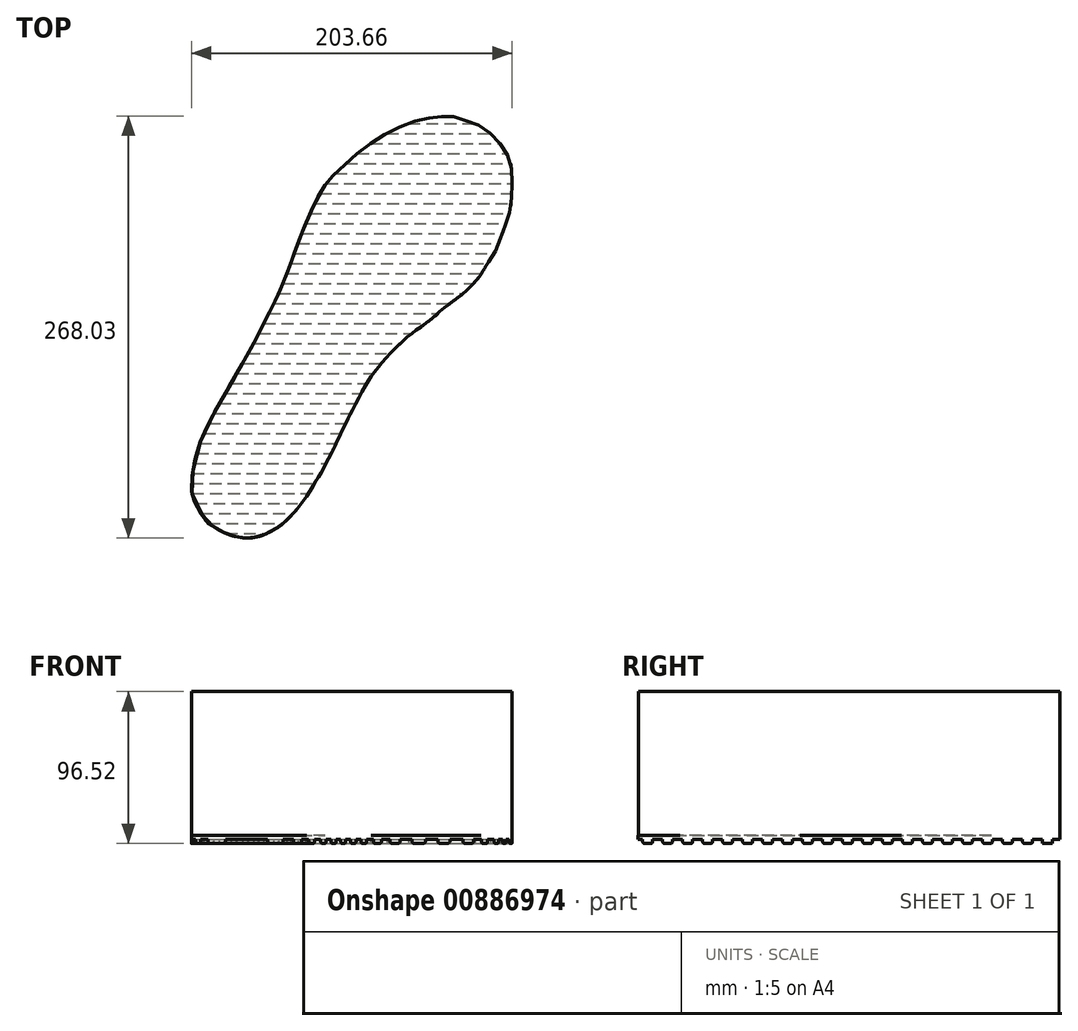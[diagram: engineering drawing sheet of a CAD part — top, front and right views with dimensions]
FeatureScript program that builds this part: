
annotation { "Feature Type Name" : "Feature", "Feature Type Description" : "" }
export const myFeature = defineFeature(function(context is Context, id is Id, definition is map)
    precondition{}
    {
        {
            var Q0;
            Q0=qCreatedBy(makeId("Top.planeOp"),FACE);
            var sketch = newSketch(context, id + "F0", { "sketchPlane" : qUnion([Q0])});
            skFitSpline(sketch, "E0", {"points": [v(-87.49, -126.78) * mm, v(-95.34, -113.93) * mm, v(-97.48, -103.22) * mm, v(-93.91, -82.03) * mm, v(-82.72, -56.56) * mm, v(-60.51, -17.71) * mm, v(-48.19, 6.35) * mm, v(-42.02, 18.83) * mm, v(-35.12, 35.9) * mm, v(-32.8, 42.2) * mm, v(-28.1, 54.9) * mm, v(-20.16, 73.8) * mm, v(-11.85, 88.53) * mm, v(-5.8, 94.95) * mm, v(5.91, 105.91) * mm, v(19.14, 115.74) * mm, v(32.74, 123.3) * mm, v(47.86, 128.96) * mm, v(57.68, 130.48) * mm, v(66.37, 131.23) * mm, v(75.06, 128.96) * mm, v(84.89, 125.56) * mm, v(94.34, 118.38) * mm, v(101.52, 109.7) * mm, v(105.67, 99.11) * mm, v(106.05, 86.64) * mm, v(105.3, 73.8) * mm, v(101.9, 61.7) * mm, v(97.74, 50.74) * mm, v(94.71, 43.94) * mm, v(89.8, 36.38) * mm, v(86.4, 30.71) * mm, v(78.68, 21.82) * mm, v(69.81, 14.52) * mm, v(62.51, 9.05) * mm, v(56.46, 3.57) * mm, v(49.99, -1.29) * mm, v(44.2, -5.6) * mm, v(38.26, -10.32) * mm, v(28.4, -19.8) * mm, v(23.09, -25.98) * mm, v(18.2, -32.02) * mm, v(14.32, -37.76) * mm, v(9.14, -47.04) * mm, v(4.13, -56.7) * mm, v(1.62, -61.71) * mm, v(-3.47, -72.08) * mm, v(-6.45, -78.5) * mm, v(-11.83, -88.97) * mm, v(-14.62, -94.55) * mm, v(-18.08, -99.93) * mm, v(-21.63, -106.17) * mm, v(-27.28, -114.4) * mm, v(-31.9, -120.26) * mm, v(-35.78, -124.24) * mm, v(-39.76, -127.85) * mm, v(-42.02, -129.57) * mm, v(-47.28, -132.82) * mm, v(-50.53, -134.39) * mm, v(-53.31, -135.42) * mm, v(-55.7, -135.96) * mm, v(-58.14, -136.5) * mm, v(-60.2, -136.64) * mm, v(-62.93, -136.75) * mm, v(-65.28, -136.57) * mm, v(-69, -135.92) * mm, v(-72.32, -135.07) * mm, v(-76.32, -133.55) * mm, v(-79.8, -131.88) * mm, v(-84.38, -128.96) * mm, v(-87.49, -126.78) * mm]});
            skSolve(sketch);
        }
        {
            var Q0;
            Q0=makeQuery(id+"F0.imprint","IMPRINT",FACE,{"disambiguationData":[TD([[makeQuery(id+"F0.imprint","IMPRINT",EDGE,{"derivedFrom":sQuery(id+"F0.wireOp",EDGE,"E0")}),-1.0]])]});
            extrude(context, id + "F1", {"entities" : qUnion([Q0]), "depth" : 91.44 * mm, "offsetDistance" : 25.4 * mm});
        }
        {
            var Q0;
            Q0=makeQuery(id+"F1.opExtrude","CAP_FACE",FACE,{"disambiguationData":[OSD([sQuery(id+"F0.wireOp",EDGE,"E0")])],"isStart":true});
            var sketch = newSketch(context, id + "F2", { "sketchPlane" : qUnion([Q0])});
            skLineSegment(sketch, "E1.bottom", {"start": v(-129.53, 140.32) * mm, "end": v(138.04, 140.32) * mm});
            skLineSegment(sketch, "E1.top", {"start": v(-129.53, -136.3) * mm, "end": v(138.04, -136.3) * mm});
            skLineSegment(sketch, "E1.left", {"start": v(-129.53, 140.32) * mm, "end": v(-129.53, -136.3) * mm});
            skLineSegment(sketch, "E1.right", {"start": v(138.04, 140.32) * mm, "end": v(138.04, -136.3) * mm});
            skSolve(sketch);
        }
        {
            var Q0;
            Q0 = qSketchRegion(id + "F2", true);
            extrude(context, id + "F3", {"entities" : qUnion([Q0]), "operationType" : NewBodyOperationType.ADD, "depth" : 5.08 * mm, "offsetDistance" : 25.4 * mm});
        }
        {
            var Q0;
            Q0=qCreatedBy(makeId("Top.planeOp"),FACE);
            cPlane(context, id + "F4", {"entities" : qUnion([Q0]), "cplaneType" : CPlaneType.OFFSET, "offset" : 5.08 * mm, "oppositeDirection" : true, "width" : 152.4 * mm, "height" : 152.4 * mm});
        }
        {
            var Q0;
            Q0=qCreatedBy(id+"F4.planeOp",FACE);
            var sketch = newSketch(context, id + "F5", { "sketchPlane" : qUnion([Q0])});
            skFitSpline(sketch, "E2", {"points": [v(-87.6, -126.95) * mm, v(-95.45, -114.1) * mm, v(-97.6, -103.38) * mm, v(-94.03, -82.2) * mm, v(-82.84, -56.72) * mm, v(-60.63, -17.88) * mm, v(-48.3, 6.19) * mm, v(-42.13, 18.66) * mm, v(-35.24, 35.73) * mm, v(-32.9, 42.03) * mm, v(-28.21, 54.74) * mm, v(-20.28, 73.63) * mm, v(-11.96, 88.37) * mm, v(-5.92, 94.8) * mm, v(5.8, 105.75) * mm, v(19.02, 115.58) * mm, v(32.63, 123.13) * mm, v(47.74, 128.8) * mm, v(57.57, 130.31) * mm, v(66.26, 131.07) * mm, v(74.95, 128.8) * mm, v(84.78, 125.4) * mm, v(94.22, 118.22) * mm, v(101.4, 109.53) * mm, v(105.56, 98.95) * mm, v(105.94, 86.48) * mm, v(105.18, 73.63) * mm, v(101.78, 61.54) * mm, v(97.62, 50.58) * mm, v(94.6, 43.78) * mm, v(89.69, 36.22) * mm, v(86.29, 30.55) * mm, v(78.56, 21.66) * mm, v(69.7, 14.36) * mm, v(62.4, 8.88) * mm, v(56.35, 3.4) * mm, v(49.87, -1.45) * mm, v(44.08, -5.77) * mm, v(38.14, -10.49) * mm, v(28.3, -19.97) * mm, v(22.97, -26.15) * mm, v(18.09, -32.18) * mm, v(14.21, -37.93) * mm, v(9.03, -47.2) * mm, v(4.02, -56.87) * mm, v(1.5, -61.88) * mm, v(-3.59, -72.25) * mm, v(-6.56, -78.67) * mm, v(-11.94, -89.14) * mm, v(-14.73, -94.71) * mm, v(-18.19, -100.1) * mm, v(-21.74, -106.34) * mm, v(-27.4, -114.56) * mm, v(-32.01, -120.42) * mm, v(-35.9, -124.4) * mm, v(-39.87, -128.01) * mm, v(-42.13, -129.73) * mm, v(-47.39, -132.98) * mm, v(-50.64, -134.55) * mm, v(-53.43, -135.59) * mm, v(-55.82, -136.12) * mm, v(-58.25, -136.66) * mm, v(-60.32, -136.8) * mm, v(-63.04, -136.9) * mm, v(-65.4, -136.73) * mm, v(-69.11, -136.09) * mm, v(-72.43, -135.23) * mm, v(-76.44, -133.71) * mm, v(-79.9, -132.04) * mm, v(-84.49, -129.12) * mm, v(-87.6, -126.95) * mm]});
            skSolve(sketch);
        }
        {
            var Q0;
            Q0 = qSketchRegion(id + "F5", true);
            extrude(context, id + "F6", {"entities" : qUnion([Q0]), "operationType" : NewBodyOperationType.INTERSECT, "endBound" : BoundingType.UP_TO_NEXT, "depth" : 5.08 * mm, "offsetDistance" : 25.4 * mm});
        }
        {
            var Q0;
            Q0=makeQuery(id+"F3.opExtrude","CAP_FACE",FACE,{"disambiguationData":[OSD([sQuery(id+"F2.wireOp",EDGE,"E1.bottom"),sQuery(id+"F2.wireOp",EDGE,"E1.top"),sQuery(id+"F2.wireOp",EDGE,"E1.left"),sQuery(id+"F2.wireOp",EDGE,"E1.right")])],"isStart":false});
            var sketch = newSketch(context, id + "F7", { "sketchPlane" : qUnion([Q0])});
            skLineSegment(sketch, "E3.bottom", {"start": v(-129.53, 140.32) * mm, "end": v(138.04, 140.32) * mm});
            skLineSegment(sketch, "E3.top", {"start": v(-129.53, 133.97) * mm, "end": v(138.04, 133.97) * mm});
            skLineSegment(sketch, "E3.left", {"start": v(-129.53, 140.32) * mm, "end": v(-129.53, 133.97) * mm});
            skLineSegment(sketch, "E3.right", {"start": v(138.04, 140.32) * mm, "end": v(138.04, 133.97) * mm});
            skLineSegment(sketch, "E4.0.1.0", {"start": v(-129.53, 127.62) * mm, "end": v(138.04, 127.62) * mm});
            skLineSegment(sketch, "E4.0.1.1", {"start": v(-129.53, 121.27) * mm, "end": v(138.04, 121.27) * mm});
            skLineSegment(sketch, "E4.0.1.2", {"start": v(138.04, 127.62) * mm, "end": v(138.04, 121.27) * mm});
            skLineSegment(sketch, "E4.0.1.3", {"start": v(-129.53, 127.62) * mm, "end": v(-129.53, 121.27) * mm});
            skLineSegment(sketch, "E4.0.2.0", {"start": v(-129.53, 114.92) * mm, "end": v(138.04, 114.92) * mm});
            skLineSegment(sketch, "E4.0.2.1", {"start": v(-129.53, 108.57) * mm, "end": v(138.04, 108.57) * mm});
            skLineSegment(sketch, "E4.0.2.2", {"start": v(138.04, 114.92) * mm, "end": v(138.04, 108.57) * mm});
            skLineSegment(sketch, "E4.0.2.3", {"start": v(-129.53, 114.92) * mm, "end": v(-129.53, 108.57) * mm});
            skLineSegment(sketch, "E4.0.3.0", {"start": v(-129.53, 102.22) * mm, "end": v(138.04, 102.22) * mm});
            skLineSegment(sketch, "E4.0.3.1", {"start": v(-129.53, 95.87) * mm, "end": v(138.04, 95.87) * mm});
            skLineSegment(sketch, "E4.0.3.2", {"start": v(138.04, 102.22) * mm, "end": v(138.04, 95.87) * mm});
            skLineSegment(sketch, "E4.0.3.3", {"start": v(-129.53, 102.22) * mm, "end": v(-129.53, 95.87) * mm});
            skLineSegment(sketch, "E4.0.4.0", {"start": v(-129.53, 89.52) * mm, "end": v(138.04, 89.52) * mm});
            skLineSegment(sketch, "E4.0.4.1", {"start": v(-129.53, 83.17) * mm, "end": v(138.04, 83.17) * mm});
            skLineSegment(sketch, "E4.0.4.2", {"start": v(138.04, 89.52) * mm, "end": v(138.04, 83.17) * mm});
            skLineSegment(sketch, "E4.0.4.3", {"start": v(-129.53, 89.52) * mm, "end": v(-129.53, 83.17) * mm});
            skLineSegment(sketch, "E4.0.5.0", {"start": v(-129.53, 76.82) * mm, "end": v(138.04, 76.82) * mm});
            skLineSegment(sketch, "E4.0.5.1", {"start": v(-129.53, 70.47) * mm, "end": v(138.04, 70.47) * mm});
            skLineSegment(sketch, "E4.0.5.2", {"start": v(138.04, 76.82) * mm, "end": v(138.04, 70.47) * mm});
            skLineSegment(sketch, "E4.0.5.3", {"start": v(-129.53, 76.82) * mm, "end": v(-129.53, 70.47) * mm});
            skLineSegment(sketch, "E4.0.6.0", {"start": v(-129.53, 64.12) * mm, "end": v(138.04, 64.12) * mm});
            skLineSegment(sketch, "E4.0.6.1", {"start": v(-129.53, 57.77) * mm, "end": v(138.04, 57.77) * mm});
            skLineSegment(sketch, "E4.0.6.2", {"start": v(138.04, 64.12) * mm, "end": v(138.04, 57.77) * mm});
            skLineSegment(sketch, "E4.0.6.3", {"start": v(-129.53, 64.12) * mm, "end": v(-129.53, 57.77) * mm});
            skLineSegment(sketch, "E4.0.7.0", {"start": v(-129.53, 51.42) * mm, "end": v(138.04, 51.42) * mm});
            skLineSegment(sketch, "E4.0.7.1", {"start": v(-129.53, 45.07) * mm, "end": v(138.04, 45.07) * mm});
            skLineSegment(sketch, "E4.0.7.2", {"start": v(138.04, 51.42) * mm, "end": v(138.04, 45.07) * mm});
            skLineSegment(sketch, "E4.0.7.3", {"start": v(-129.53, 51.42) * mm, "end": v(-129.53, 45.07) * mm});
            skLineSegment(sketch, "E4.0.8.0", {"start": v(-129.53, 38.72) * mm, "end": v(138.04, 38.72) * mm});
            skLineSegment(sketch, "E4.0.8.1", {"start": v(-129.53, 32.37) * mm, "end": v(138.04, 32.37) * mm});
            skLineSegment(sketch, "E4.0.8.2", {"start": v(138.04, 38.72) * mm, "end": v(138.04, 32.37) * mm});
            skLineSegment(sketch, "E4.0.8.3", {"start": v(-129.53, 38.72) * mm, "end": v(-129.53, 32.37) * mm});
            skLineSegment(sketch, "E4.0.9.0", {"start": v(-129.53, 26.02) * mm, "end": v(138.04, 26.02) * mm});
            skLineSegment(sketch, "E4.0.9.1", {"start": v(-129.53, 19.67) * mm, "end": v(138.04, 19.67) * mm});
            skLineSegment(sketch, "E4.0.9.2", {"start": v(138.04, 26.02) * mm, "end": v(138.04, 19.67) * mm});
            skLineSegment(sketch, "E4.0.9.3", {"start": v(-129.53, 26.02) * mm, "end": v(-129.53, 19.67) * mm});
            skLineSegment(sketch, "E4.0.10.0", {"start": v(-129.53, 13.32) * mm, "end": v(138.04, 13.32) * mm});
            skLineSegment(sketch, "E4.0.10.1", {"start": v(-129.53, 6.97) * mm, "end": v(138.04, 6.97) * mm});
            skLineSegment(sketch, "E4.0.10.2", {"start": v(138.04, 13.32) * mm, "end": v(138.04, 6.97) * mm});
            skLineSegment(sketch, "E4.0.10.3", {"start": v(-129.53, 13.32) * mm, "end": v(-129.53, 6.97) * mm});
            skLineSegment(sketch, "E4.0.11.0", {"start": v(-129.53, 0.62) * mm, "end": v(138.04, 0.62) * mm});
            skLineSegment(sketch, "E4.0.11.1", {"start": v(-129.53, -5.73) * mm, "end": v(138.04, -5.73) * mm});
            skLineSegment(sketch, "E4.0.11.2", {"start": v(138.04, 0.62) * mm, "end": v(138.04, -5.73) * mm});
            skLineSegment(sketch, "E4.0.11.3", {"start": v(-129.53, 0.62) * mm, "end": v(-129.53, -5.73) * mm});
            skLineSegment(sketch, "E4.0.12.0", {"start": v(-129.53, -12.08) * mm, "end": v(138.04, -12.08) * mm});
            skLineSegment(sketch, "E4.0.12.1", {"start": v(-129.53, -18.43) * mm, "end": v(138.04, -18.43) * mm});
            skLineSegment(sketch, "E4.0.12.2", {"start": v(138.04, -12.08) * mm, "end": v(138.04, -18.43) * mm});
            skLineSegment(sketch, "E4.0.12.3", {"start": v(-129.53, -12.08) * mm, "end": v(-129.53, -18.43) * mm});
            skLineSegment(sketch, "E4.0.13.0", {"start": v(-129.53, -24.78) * mm, "end": v(138.04, -24.78) * mm});
            skLineSegment(sketch, "E4.0.13.1", {"start": v(-129.53, -31.13) * mm, "end": v(138.04, -31.13) * mm});
            skLineSegment(sketch, "E4.0.13.2", {"start": v(138.04, -24.78) * mm, "end": v(138.04, -31.13) * mm});
            skLineSegment(sketch, "E4.0.13.3", {"start": v(-129.53, -24.78) * mm, "end": v(-129.53, -31.13) * mm});
            skLineSegment(sketch, "E4.0.14.0", {"start": v(-129.53, -37.48) * mm, "end": v(138.04, -37.48) * mm});
            skLineSegment(sketch, "E4.0.14.1", {"start": v(-129.53, -43.83) * mm, "end": v(138.04, -43.83) * mm});
            skLineSegment(sketch, "E4.0.14.2", {"start": v(138.04, -37.48) * mm, "end": v(138.04, -43.83) * mm});
            skLineSegment(sketch, "E4.0.14.3", {"start": v(-129.53, -37.48) * mm, "end": v(-129.53, -43.83) * mm});
            skLineSegment(sketch, "E4.0.15.0", {"start": v(-129.53, -50.18) * mm, "end": v(138.04, -50.18) * mm});
            skLineSegment(sketch, "E4.0.15.1", {"start": v(-129.53, -56.53) * mm, "end": v(138.04, -56.53) * mm});
            skLineSegment(sketch, "E4.0.15.2", {"start": v(138.04, -50.18) * mm, "end": v(138.04, -56.53) * mm});
            skLineSegment(sketch, "E4.0.15.3", {"start": v(-129.53, -50.18) * mm, "end": v(-129.53, -56.53) * mm});
            skLineSegment(sketch, "E4.0.16.0", {"start": v(-129.53, -62.88) * mm, "end": v(138.04, -62.88) * mm});
            skLineSegment(sketch, "E4.0.16.1", {"start": v(-129.53, -69.23) * mm, "end": v(138.04, -69.23) * mm});
            skLineSegment(sketch, "E4.0.16.2", {"start": v(138.04, -62.88) * mm, "end": v(138.04, -69.23) * mm});
            skLineSegment(sketch, "E4.0.16.3", {"start": v(-129.53, -62.88) * mm, "end": v(-129.53, -69.23) * mm});
            skLineSegment(sketch, "E4.0.17.0", {"start": v(-129.53, -75.58) * mm, "end": v(138.04, -75.58) * mm});
            skLineSegment(sketch, "E4.0.17.1", {"start": v(-129.53, -81.93) * mm, "end": v(138.04, -81.93) * mm});
            skLineSegment(sketch, "E4.0.17.2", {"start": v(138.04, -75.58) * mm, "end": v(138.04, -81.93) * mm});
            skLineSegment(sketch, "E4.0.17.3", {"start": v(-129.53, -75.58) * mm, "end": v(-129.53, -81.93) * mm});
            skLineSegment(sketch, "E4.0.18.0", {"start": v(-129.53, -88.28) * mm, "end": v(138.04, -88.28) * mm});
            skLineSegment(sketch, "E4.0.18.1", {"start": v(-129.53, -94.63) * mm, "end": v(138.04, -94.63) * mm});
            skLineSegment(sketch, "E4.0.18.2", {"start": v(138.04, -88.28) * mm, "end": v(138.04, -94.63) * mm});
            skLineSegment(sketch, "E4.0.18.3", {"start": v(-129.53, -88.28) * mm, "end": v(-129.53, -94.63) * mm});
            skLineSegment(sketch, "E4.0.19.0", {"start": v(-129.53, -100.98) * mm, "end": v(138.04, -100.98) * mm});
            skLineSegment(sketch, "E4.0.19.1", {"start": v(-129.53, -107.33) * mm, "end": v(138.04, -107.33) * mm});
            skLineSegment(sketch, "E4.0.19.2", {"start": v(138.04, -100.98) * mm, "end": v(138.04, -107.33) * mm});
            skLineSegment(sketch, "E4.0.19.3", {"start": v(-129.53, -100.98) * mm, "end": v(-129.53, -107.33) * mm});
            skLineSegment(sketch, "E4.0.20.0", {"start": v(-129.53, -113.68) * mm, "end": v(138.04, -113.68) * mm});
            skLineSegment(sketch, "E4.0.20.1", {"start": v(-129.53, -120.03) * mm, "end": v(138.04, -120.03) * mm});
            skLineSegment(sketch, "E4.0.20.2", {"start": v(138.04, -113.68) * mm, "end": v(138.04, -120.03) * mm});
            skLineSegment(sketch, "E4.0.20.3", {"start": v(-129.53, -113.68) * mm, "end": v(-129.53, -120.03) * mm});
            skLineSegment(sketch, "E4.0.21.0", {"start": v(-129.53, -126.38) * mm, "end": v(138.04, -126.38) * mm});
            skLineSegment(sketch, "E4.0.21.1", {"start": v(-129.53, -132.73) * mm, "end": v(138.04, -132.73) * mm});
            skLineSegment(sketch, "E4.0.21.2", {"start": v(138.04, -126.38) * mm, "end": v(138.04, -132.73) * mm});
            skLineSegment(sketch, "E4.0.21.3", {"start": v(-129.53, -126.38) * mm, "end": v(-129.53, -132.73) * mm});
            skLineSegment(sketch, "E4.0.22.0", {"start": v(-129.53, -139.08) * mm, "end": v(138.04, -139.08) * mm});
            skLineSegment(sketch, "E4.0.22.1", {"start": v(-129.53, -145.43) * mm, "end": v(138.04, -145.43) * mm});
            skLineSegment(sketch, "E4.0.22.2", {"start": v(138.04, -139.08) * mm, "end": v(138.04, -145.43) * mm});
            skLineSegment(sketch, "E4.0.22.3", {"start": v(-129.53, -139.08) * mm, "end": v(-129.53, -145.43) * mm});
            skLineSegment(sketch, "E4.0.23.0", {"start": v(-129.53, -151.78) * mm, "end": v(138.04, -151.78) * mm});
            skLineSegment(sketch, "E4.0.23.1", {"start": v(-129.53, -158.13) * mm, "end": v(138.04, -158.13) * mm});
            skLineSegment(sketch, "E4.0.23.2", {"start": v(138.04, -151.78) * mm, "end": v(138.04, -158.13) * mm});
            skLineSegment(sketch, "E4.0.23.3", {"start": v(-129.53, -151.78) * mm, "end": v(-129.53, -158.13) * mm});
            skLineSegment(sketch, "E4.0.24.0", {"start": v(-129.53, -164.48) * mm, "end": v(138.04, -164.48) * mm});
            skLineSegment(sketch, "E4.0.24.1", {"start": v(-129.53, -170.83) * mm, "end": v(138.04, -170.83) * mm});
            skLineSegment(sketch, "E4.0.24.2", {"start": v(138.04, -164.48) * mm, "end": v(138.04, -170.83) * mm});
            skLineSegment(sketch, "E4.0.24.3", {"start": v(-129.53, -164.48) * mm, "end": v(-129.53, -170.83) * mm});
            skLineSegment(sketch, "E4.0.25.0", {"start": v(-129.53, -177.18) * mm, "end": v(138.04, -177.18) * mm});
            skLineSegment(sketch, "E4.0.25.1", {"start": v(-129.53, -183.53) * mm, "end": v(138.04, -183.53) * mm});
            skLineSegment(sketch, "E4.0.25.2", {"start": v(138.04, -177.18) * mm, "end": v(138.04, -183.53) * mm});
            skLineSegment(sketch, "E4.0.25.3", {"start": v(-129.53, -177.18) * mm, "end": v(-129.53, -183.53) * mm});
            skLineSegment(sketch, "E4.0.26.0", {"start": v(-129.53, -189.88) * mm, "end": v(138.04, -189.88) * mm});
            skLineSegment(sketch, "E4.0.26.1", {"start": v(-129.53, -196.23) * mm, "end": v(138.04, -196.23) * mm});
            skLineSegment(sketch, "E4.0.26.2", {"start": v(138.04, -189.88) * mm, "end": v(138.04, -196.23) * mm});
            skLineSegment(sketch, "E4.0.26.3", {"start": v(-129.53, -189.88) * mm, "end": v(-129.53, -196.23) * mm});
            skLineSegment(sketch, "E4.0.27.0", {"start": v(-129.53, -202.58) * mm, "end": v(138.04, -202.58) * mm});
            skLineSegment(sketch, "E4.0.27.1", {"start": v(-129.53, -208.93) * mm, "end": v(138.04, -208.93) * mm});
            skLineSegment(sketch, "E4.0.27.2", {"start": v(138.04, -202.58) * mm, "end": v(138.04, -208.93) * mm});
            skLineSegment(sketch, "E4.0.27.3", {"start": v(-129.53, -202.58) * mm, "end": v(-129.53, -208.93) * mm});
            skLineSegment(sketch, "E4.0.28.0", {"start": v(-129.53, -215.28) * mm, "end": v(138.04, -215.28) * mm});
            skLineSegment(sketch, "E4.0.28.1", {"start": v(-129.53, -221.63) * mm, "end": v(138.04, -221.63) * mm});
            skLineSegment(sketch, "E4.0.28.2", {"start": v(138.04, -215.28) * mm, "end": v(138.04, -221.63) * mm});
            skLineSegment(sketch, "E4.0.28.3", {"start": v(-129.53, -215.28) * mm, "end": v(-129.53, -221.63) * mm});
            skLineSegment(sketch, "E4.0.29.0", {"start": v(-129.53, -227.98) * mm, "end": v(138.04, -227.98) * mm});
            skLineSegment(sketch, "E4.0.29.1", {"start": v(-129.53, -234.33) * mm, "end": v(138.04, -234.33) * mm});
            skLineSegment(sketch, "E4.0.29.2", {"start": v(138.04, -227.98) * mm, "end": v(138.04, -234.33) * mm});
            skLineSegment(sketch, "E4.0.29.3", {"start": v(-129.53, -227.98) * mm, "end": v(-129.53, -234.33) * mm});
            skLineSegment(sketch, "E4.0.30.0", {"start": v(-129.53, -240.68) * mm, "end": v(138.04, -240.68) * mm});
            skLineSegment(sketch, "E4.0.30.1", {"start": v(-129.53, -247.03) * mm, "end": v(138.04, -247.03) * mm});
            skLineSegment(sketch, "E4.0.30.2", {"start": v(138.04, -240.68) * mm, "end": v(138.04, -247.03) * mm});
            skLineSegment(sketch, "E4.0.30.3", {"start": v(-129.53, -240.68) * mm, "end": v(-129.53, -247.03) * mm});
            skLineSegment(sketch, "E4.0.31.0", {"start": v(-129.53, -253.38) * mm, "end": v(138.04, -253.38) * mm});
            skLineSegment(sketch, "E4.0.31.1", {"start": v(-129.53, -259.73) * mm, "end": v(138.04, -259.73) * mm});
            skLineSegment(sketch, "E4.0.31.2", {"start": v(138.04, -253.38) * mm, "end": v(138.04, -259.73) * mm});
            skLineSegment(sketch, "E4.0.31.3", {"start": v(-129.53, -253.38) * mm, "end": v(-129.53, -259.73) * mm});
            skLineSegment(sketch, "E4.0.32.0", {"start": v(-129.53, -266.08) * mm, "end": v(138.04, -266.08) * mm});
            skLineSegment(sketch, "E4.0.32.1", {"start": v(-129.53, -272.43) * mm, "end": v(138.04, -272.43) * mm});
            skLineSegment(sketch, "E4.0.32.2", {"start": v(138.04, -266.08) * mm, "end": v(138.04, -272.43) * mm});
            skLineSegment(sketch, "E4.0.32.3", {"start": v(-129.53, -266.08) * mm, "end": v(-129.53, -272.43) * mm});
            skLineSegment(sketch, "E4.0.33.0", {"start": v(-129.53, -278.78) * mm, "end": v(138.04, -278.78) * mm});
            skLineSegment(sketch, "E4.0.33.1", {"start": v(-129.53, -285.13) * mm, "end": v(138.04, -285.13) * mm});
            skLineSegment(sketch, "E4.0.33.2", {"start": v(138.04, -278.78) * mm, "end": v(138.04, -285.13) * mm});
            skLineSegment(sketch, "E4.0.33.3", {"start": v(-129.53, -278.78) * mm, "end": v(-129.53, -285.13) * mm});
            skLineSegment(sketch, "E4.0.34.0", {"start": v(-129.53, -291.48) * mm, "end": v(138.04, -291.48) * mm});
            skLineSegment(sketch, "E4.0.34.1", {"start": v(-129.53, -297.83) * mm, "end": v(138.04, -297.83) * mm});
            skLineSegment(sketch, "E4.0.34.2", {"start": v(138.04, -291.48) * mm, "end": v(138.04, -297.83) * mm});
            skLineSegment(sketch, "E4.0.34.3", {"start": v(-129.53, -291.48) * mm, "end": v(-129.53, -297.83) * mm});
            skLineSegment(sketch, "E4.0.35.0", {"start": v(-129.53, -304.18) * mm, "end": v(138.04, -304.18) * mm});
            skLineSegment(sketch, "E4.0.35.1", {"start": v(-129.53, -310.53) * mm, "end": v(138.04, -310.53) * mm});
            skLineSegment(sketch, "E4.0.35.2", {"start": v(138.04, -304.18) * mm, "end": v(138.04, -310.53) * mm});
            skLineSegment(sketch, "E4.0.35.3", {"start": v(-129.53, -304.18) * mm, "end": v(-129.53, -310.53) * mm});
            skLineSegment(sketch, "E4.0.36.0", {"start": v(-129.53, -316.88) * mm, "end": v(138.04, -316.88) * mm});
            skLineSegment(sketch, "E4.0.36.1", {"start": v(-129.53, -323.23) * mm, "end": v(138.04, -323.23) * mm});
            skLineSegment(sketch, "E4.0.36.2", {"start": v(138.04, -316.88) * mm, "end": v(138.04, -323.23) * mm});
            skLineSegment(sketch, "E4.0.36.3", {"start": v(-129.53, -316.88) * mm, "end": v(-129.53, -323.23) * mm});
            skLineSegment(sketch, "E4.0.37.0", {"start": v(-129.53, -329.58) * mm, "end": v(138.04, -329.58) * mm});
            skLineSegment(sketch, "E4.0.37.1", {"start": v(-129.53, -335.93) * mm, "end": v(138.04, -335.93) * mm});
            skLineSegment(sketch, "E4.0.37.2", {"start": v(138.04, -329.58) * mm, "end": v(138.04, -335.93) * mm});
            skLineSegment(sketch, "E4.0.37.3", {"start": v(-129.53, -329.58) * mm, "end": v(-129.53, -335.93) * mm});
            skLineSegment(sketch, "E4.0.38.0", {"start": v(-129.53, -342.28) * mm, "end": v(138.04, -342.28) * mm});
            skLineSegment(sketch, "E4.0.38.1", {"start": v(-129.53, -348.63) * mm, "end": v(138.04, -348.63) * mm});
            skLineSegment(sketch, "E4.0.38.2", {"start": v(138.04, -342.28) * mm, "end": v(138.04, -348.63) * mm});
            skLineSegment(sketch, "E4.0.38.3", {"start": v(-129.53, -342.28) * mm, "end": v(-129.53, -348.63) * mm});
            skLineSegment(sketch, "E4.0.39.0", {"start": v(-129.53, -354.98) * mm, "end": v(138.04, -354.98) * mm});
            skLineSegment(sketch, "E4.0.39.1", {"start": v(-129.53, -361.33) * mm, "end": v(138.04, -361.33) * mm});
            skLineSegment(sketch, "E4.0.39.2", {"start": v(138.04, -354.98) * mm, "end": v(138.04, -361.33) * mm});
            skLineSegment(sketch, "E4.0.39.3", {"start": v(-129.53, -354.98) * mm, "end": v(-129.53, -361.33) * mm});
            skLineSegment(sketch, "E4.0.40.0", {"start": v(-129.53, -367.68) * mm, "end": v(138.04, -367.68) * mm});
            skLineSegment(sketch, "E4.0.40.1", {"start": v(-129.53, -374.03) * mm, "end": v(138.04, -374.03) * mm});
            skLineSegment(sketch, "E4.0.40.2", {"start": v(138.04, -367.68) * mm, "end": v(138.04, -374.03) * mm});
            skLineSegment(sketch, "E4.0.40.3", {"start": v(-129.53, -367.68) * mm, "end": v(-129.53, -374.03) * mm});
            skLineSegment(sketch, "E4.0.41.0", {"start": v(-129.53, -380.38) * mm, "end": v(138.04, -380.38) * mm});
            skLineSegment(sketch, "E4.0.41.1", {"start": v(-129.53, -386.73) * mm, "end": v(138.04, -386.73) * mm});
            skLineSegment(sketch, "E4.0.41.2", {"start": v(138.04, -380.38) * mm, "end": v(138.04, -386.73) * mm});
            skLineSegment(sketch, "E4.0.41.3", {"start": v(-129.53, -380.38) * mm, "end": v(-129.53, -386.73) * mm});
            skLineSegment(sketch, "E4.0.42.0", {"start": v(-129.53, -393.08) * mm, "end": v(138.04, -393.08) * mm});
            skLineSegment(sketch, "E4.0.42.1", {"start": v(-129.53, -399.43) * mm, "end": v(138.04, -399.43) * mm});
            skLineSegment(sketch, "E4.0.42.2", {"start": v(138.04, -393.08) * mm, "end": v(138.04, -399.43) * mm});
            skLineSegment(sketch, "E4.0.42.3", {"start": v(-129.53, -393.08) * mm, "end": v(-129.53, -399.43) * mm});
            skLineSegment(sketch, "E4.0.43.0", {"start": v(-129.53, -405.78) * mm, "end": v(138.04, -405.78) * mm});
            skLineSegment(sketch, "E4.0.43.1", {"start": v(-129.53, -412.13) * mm, "end": v(138.04, -412.13) * mm});
            skLineSegment(sketch, "E4.0.43.2", {"start": v(138.04, -405.78) * mm, "end": v(138.04, -412.13) * mm});
            skLineSegment(sketch, "E4.0.43.3", {"start": v(-129.53, -405.78) * mm, "end": v(-129.53, -412.13) * mm});
            skLineSegment(sketch, "E4.0.44.0", {"start": v(-129.53, -418.48) * mm, "end": v(138.04, -418.48) * mm});
            skLineSegment(sketch, "E4.0.44.1", {"start": v(-129.53, -424.83) * mm, "end": v(138.04, -424.83) * mm});
            skLineSegment(sketch, "E4.0.44.2", {"start": v(138.04, -418.48) * mm, "end": v(138.04, -424.83) * mm});
            skLineSegment(sketch, "E4.0.44.3", {"start": v(-129.53, -418.48) * mm, "end": v(-129.53, -424.83) * mm});
            skLineSegment(sketch, "E4.0.45.0", {"start": v(-129.53, -431.18) * mm, "end": v(138.04, -431.18) * mm});
            skLineSegment(sketch, "E4.0.45.1", {"start": v(-129.53, -437.53) * mm, "end": v(138.04, -437.53) * mm});
            skLineSegment(sketch, "E4.0.45.2", {"start": v(138.04, -431.18) * mm, "end": v(138.04, -437.53) * mm});
            skLineSegment(sketch, "E4.0.45.3", {"start": v(-129.53, -431.18) * mm, "end": v(-129.53, -437.53) * mm});
            skLineSegment(sketch, "E4.0.46.0", {"start": v(-129.53, -443.88) * mm, "end": v(138.04, -443.88) * mm});
            skLineSegment(sketch, "E4.0.46.1", {"start": v(-129.53, -450.23) * mm, "end": v(138.04, -450.23) * mm});
            skLineSegment(sketch, "E4.0.46.2", {"start": v(138.04, -443.88) * mm, "end": v(138.04, -450.23) * mm});
            skLineSegment(sketch, "E4.0.46.3", {"start": v(-129.53, -443.88) * mm, "end": v(-129.53, -450.23) * mm});
            skLineSegment(sketch, "E4.0.47.0", {"start": v(-129.53, -456.58) * mm, "end": v(138.04, -456.58) * mm});
            skLineSegment(sketch, "E4.0.47.1", {"start": v(-129.53, -462.93) * mm, "end": v(138.04, -462.93) * mm});
            skLineSegment(sketch, "E4.0.47.2", {"start": v(138.04, -456.58) * mm, "end": v(138.04, -462.93) * mm});
            skLineSegment(sketch, "E4.0.47.3", {"start": v(-129.53, -456.58) * mm, "end": v(-129.53, -462.93) * mm});
            skLineSegment(sketch, "E4.0.48.0", {"start": v(-129.53, -469.28) * mm, "end": v(138.04, -469.28) * mm});
            skLineSegment(sketch, "E4.0.48.1", {"start": v(-129.53, -475.63) * mm, "end": v(138.04, -475.63) * mm});
            skLineSegment(sketch, "E4.0.48.2", {"start": v(138.04, -469.28) * mm, "end": v(138.04, -475.63) * mm});
            skLineSegment(sketch, "E4.0.48.3", {"start": v(-129.53, -469.28) * mm, "end": v(-129.53, -475.63) * mm});
            skLineSegment(sketch, "E4.0.49.0", {"start": v(-129.53, -481.98) * mm, "end": v(138.04, -481.98) * mm});
            skLineSegment(sketch, "E4.0.49.1", {"start": v(-129.53, -488.33) * mm, "end": v(138.04, -488.33) * mm});
            skLineSegment(sketch, "E4.0.49.2", {"start": v(138.04, -481.98) * mm, "end": v(138.04, -488.33) * mm});
            skLineSegment(sketch, "E4.0.49.3", {"start": v(-129.53, -481.98) * mm, "end": v(-129.53, -488.33) * mm});
            skLineSegment(sketch, "E4.direction1", {"start": v(-129.53, 140.32) * mm, "end": v(-104.13, 140.32) * mm, "construction": true});
            skLineSegment(sketch, "E4.direction2", {"start": v(-129.53, 140.32) * mm, "end": v(-129.53, 127.62) * mm, "construction": true});
            skSolve(sketch);
        }
        {
            var Q0;
            Q0 = qSketchRegion(id + "F7", true);
            extrude(context, id + "F8", {"entities" : qUnion([Q0]), "operationType" : NewBodyOperationType.REMOVE, "oppositeDirection" : true, "depth" : 2.54 * mm, "offsetDistance" : 25.4 * mm});
        }
        {
            var Q0;
            Q0=makeQuery(id+"F8.boolean.opBoolean","COPY",EDGE,{"derivedFrom":makeQuery(id+"F8.opExtrude","CAP_EDGE",EDGE,{"disambiguationData":[OSD([sQuery(id+"F7.wireOp",EDGE,"E4.0.21.1")])],"isStart":true})});
            var Q1;
            Q1=makeQuery(id+"F8.boolean.opBoolean","COPY",EDGE,{"derivedFrom":makeQuery(id+"F8.opExtrude","CAP_EDGE",EDGE,{"disambiguationData":[OSD([sQuery(id+"F7.wireOp",EDGE,"E4.0.20.1")])],"isStart":true})});
            var Q2;
            Q2=makeQuery(id+"F8.boolean.opBoolean","COPY",EDGE,{"derivedFrom":makeQuery(id+"F8.opExtrude","CAP_EDGE",EDGE,{"disambiguationData":[OSD([sQuery(id+"F7.wireOp",EDGE,"E4.0.21.0")])],"isStart":true})});
            var Q3;
            Q3=makeQuery(id+"F8.boolean.opBoolean","COPY",EDGE,{"derivedFrom":makeQuery(id+"F8.opExtrude","CAP_EDGE",EDGE,{"disambiguationData":[OSD([sQuery(id+"F7.wireOp",EDGE,"E4.0.20.0")])],"isStart":true})});
            var Q4;
            Q4=makeQuery(id+"F8.boolean.opBoolean","COPY",EDGE,{"derivedFrom":makeQuery(id+"F8.opExtrude","CAP_EDGE",EDGE,{"disambiguationData":[OSD([sQuery(id+"F7.wireOp",EDGE,"E4.0.19.1")])],"isStart":true})});
            var Q5;
            Q5=makeQuery(id+"F8.boolean.opBoolean","COPY",EDGE,{"derivedFrom":makeQuery(id+"F8.opExtrude","CAP_EDGE",EDGE,{"disambiguationData":[OSD([sQuery(id+"F7.wireOp",EDGE,"E4.0.19.0")])],"isStart":true})});
            var Q6;
            Q6=makeQuery(id+"F8.boolean.opBoolean","COPY",EDGE,{"derivedFrom":makeQuery(id+"F8.opExtrude","CAP_EDGE",EDGE,{"disambiguationData":[OSD([sQuery(id+"F7.wireOp",EDGE,"E4.0.18.1")])],"isStart":true})});
            var Q7;
            Q7=makeQuery(id+"F8.boolean.opBoolean","COPY",EDGE,{"derivedFrom":makeQuery(id+"F8.opExtrude","CAP_EDGE",EDGE,{"disambiguationData":[OSD([sQuery(id+"F7.wireOp",EDGE,"E4.0.16.1")])],"isStart":true})});
            var Q8;
            Q8=makeQuery(id+"F8.boolean.opBoolean","COPY",EDGE,{"derivedFrom":makeQuery(id+"F8.opExtrude","CAP_EDGE",EDGE,{"disambiguationData":[OSD([sQuery(id+"F7.wireOp",EDGE,"E4.0.17.0")])],"isStart":true})});
            var Q9;
            Q9=makeQuery(id+"F8.boolean.opBoolean","COPY",EDGE,{"derivedFrom":makeQuery(id+"F8.opExtrude","CAP_EDGE",EDGE,{"disambiguationData":[OSD([sQuery(id+"F7.wireOp",EDGE,"E4.0.17.1")])],"isStart":true})});
            var Q10;
            Q10=makeQuery(id+"F8.boolean.opBoolean","COPY",EDGE,{"derivedFrom":makeQuery(id+"F8.opExtrude","CAP_EDGE",EDGE,{"disambiguationData":[OSD([sQuery(id+"F7.wireOp",EDGE,"E4.0.18.0")])],"isStart":true})});
            var Q11;
            Q11=makeQuery(id+"F8.boolean.opBoolean","COPY",EDGE,{"derivedFrom":makeQuery(id+"F8.opExtrude","CAP_EDGE",EDGE,{"disambiguationData":[OSD([sQuery(id+"F7.wireOp",EDGE,"E4.0.16.0")])],"isStart":true})});
            var Q12;
            Q12=makeQuery(id+"F8.boolean.opBoolean","COPY",EDGE,{"derivedFrom":makeQuery(id+"F8.opExtrude","CAP_EDGE",EDGE,{"disambiguationData":[OSD([sQuery(id+"F7.wireOp",EDGE,"E4.0.15.1")])],"isStart":true})});
            var Q13;
            Q13=makeQuery(id+"F8.boolean.opBoolean","COPY",EDGE,{"derivedFrom":makeQuery(id+"F8.opExtrude","CAP_EDGE",EDGE,{"disambiguationData":[OSD([sQuery(id+"F7.wireOp",EDGE,"E4.0.15.0")])],"isStart":true})});
            var Q14;
            Q14=makeQuery(id+"F8.boolean.opBoolean","COPY",EDGE,{"derivedFrom":makeQuery(id+"F8.opExtrude","CAP_EDGE",EDGE,{"disambiguationData":[OSD([sQuery(id+"F7.wireOp",EDGE,"E4.0.14.1")])],"isStart":true})});
            var Q15;
            Q15=makeQuery(id+"F8.boolean.opBoolean","COPY",EDGE,{"derivedFrom":makeQuery(id+"F8.opExtrude","CAP_EDGE",EDGE,{"disambiguationData":[OSD([sQuery(id+"F7.wireOp",EDGE,"E4.0.14.0")])],"isStart":true})});
            var Q16;
            Q16=makeQuery(id+"F8.boolean.opBoolean","COPY",EDGE,{"derivedFrom":makeQuery(id+"F8.opExtrude","CAP_EDGE",EDGE,{"disambiguationData":[OSD([sQuery(id+"F7.wireOp",EDGE,"E4.0.13.1")])],"isStart":true})});
            var Q17;
            Q17=makeQuery(id+"F8.boolean.opBoolean","COPY",EDGE,{"derivedFrom":makeQuery(id+"F8.opExtrude","CAP_EDGE",EDGE,{"disambiguationData":[OSD([sQuery(id+"F7.wireOp",EDGE,"E4.0.13.0")])],"isStart":true})});
            var Q18;
            Q18=makeQuery(id+"F8.boolean.opBoolean","COPY",EDGE,{"derivedFrom":makeQuery(id+"F8.opExtrude","CAP_EDGE",EDGE,{"disambiguationData":[OSD([sQuery(id+"F7.wireOp",EDGE,"E4.0.12.1")])],"isStart":true})});
            var Q19;
            Q19=makeQuery(id+"F8.boolean.opBoolean","COPY",EDGE,{"derivedFrom":makeQuery(id+"F8.opExtrude","CAP_EDGE",EDGE,{"disambiguationData":[OSD([sQuery(id+"F7.wireOp",EDGE,"E4.0.12.0")])],"isStart":true})});
            var Q20;
            Q20=makeQuery(id+"F8.boolean.opBoolean","COPY",EDGE,{"derivedFrom":makeQuery(id+"F8.opExtrude","CAP_EDGE",EDGE,{"disambiguationData":[OSD([sQuery(id+"F7.wireOp",EDGE,"E4.0.11.1")])],"isStart":true})});
            var Q21;
            Q21=makeQuery(id+"F8.boolean.opBoolean","COPY",EDGE,{"derivedFrom":makeQuery(id+"F8.opExtrude","CAP_EDGE",EDGE,{"disambiguationData":[OSD([sQuery(id+"F7.wireOp",EDGE,"E4.0.11.0")])],"isStart":true})});
            var Q22;
            Q22=makeQuery(id+"F8.boolean.opBoolean","COPY",EDGE,{"derivedFrom":makeQuery(id+"F8.opExtrude","CAP_EDGE",EDGE,{"disambiguationData":[OSD([sQuery(id+"F7.wireOp",EDGE,"E4.0.10.1")])],"isStart":true})});
            var Q23;
            Q23=makeQuery(id+"F8.boolean.opBoolean","COPY",EDGE,{"derivedFrom":makeQuery(id+"F8.opExtrude","CAP_EDGE",EDGE,{"disambiguationData":[OSD([sQuery(id+"F7.wireOp",EDGE,"E4.0.10.0")])],"isStart":true})});
            var Q24;
            Q24=makeQuery(id+"F8.boolean.opBoolean","COPY",EDGE,{"derivedFrom":makeQuery(id+"F8.opExtrude","CAP_EDGE",EDGE,{"disambiguationData":[OSD([sQuery(id+"F7.wireOp",EDGE,"E4.0.9.1")])],"isStart":true})});
            var Q25;
            Q25=makeQuery(id+"F8.boolean.opBoolean","COPY",EDGE,{"derivedFrom":makeQuery(id+"F8.opExtrude","CAP_EDGE",EDGE,{"disambiguationData":[OSD([sQuery(id+"F7.wireOp",EDGE,"E4.0.9.0")])],"isStart":true})});
            var Q26;
            Q26=makeQuery(id+"F8.boolean.opBoolean","COPY",EDGE,{"derivedFrom":makeQuery(id+"F8.opExtrude","CAP_EDGE",EDGE,{"disambiguationData":[OSD([sQuery(id+"F7.wireOp",EDGE,"E4.0.8.1")])],"isStart":true})});
            var Q27;
            Q27=makeQuery(id+"F8.boolean.opBoolean","COPY",EDGE,{"derivedFrom":makeQuery(id+"F8.opExtrude","CAP_EDGE",EDGE,{"disambiguationData":[OSD([sQuery(id+"F7.wireOp",EDGE,"E4.0.8.0")])],"isStart":true})});
            var Q28;
            Q28=makeQuery(id+"F8.boolean.opBoolean","COPY",EDGE,{"derivedFrom":makeQuery(id+"F8.opExtrude","CAP_EDGE",EDGE,{"disambiguationData":[OSD([sQuery(id+"F7.wireOp",EDGE,"E4.0.7.1")])],"isStart":true})});
            var Q29;
            Q29=makeQuery(id+"F8.boolean.opBoolean","COPY",EDGE,{"derivedFrom":makeQuery(id+"F8.opExtrude","CAP_EDGE",EDGE,{"disambiguationData":[OSD([sQuery(id+"F7.wireOp",EDGE,"E4.0.7.0")])],"isStart":true})});
            var Q30;
            Q30=makeQuery(id+"F8.boolean.opBoolean","COPY",EDGE,{"derivedFrom":makeQuery(id+"F8.opExtrude","CAP_EDGE",EDGE,{"disambiguationData":[OSD([sQuery(id+"F7.wireOp",EDGE,"E4.0.6.1")])],"isStart":true})});
            var Q31;
            Q31=makeQuery(id+"F8.boolean.opBoolean","COPY",EDGE,{"derivedFrom":makeQuery(id+"F8.opExtrude","CAP_EDGE",EDGE,{"disambiguationData":[OSD([sQuery(id+"F7.wireOp",EDGE,"E4.0.6.0")])],"isStart":true})});
            var Q32;
            Q32=makeQuery(id+"F8.boolean.opBoolean","COPY",EDGE,{"derivedFrom":makeQuery(id+"F8.opExtrude","CAP_EDGE",EDGE,{"disambiguationData":[OSD([sQuery(id+"F7.wireOp",EDGE,"E4.0.5.1")])],"isStart":true})});
            var Q33;
            Q33=makeQuery(id+"F8.boolean.opBoolean","COPY",EDGE,{"derivedFrom":makeQuery(id+"F8.opExtrude","CAP_EDGE",EDGE,{"disambiguationData":[OSD([sQuery(id+"F7.wireOp",EDGE,"E4.0.5.0")])],"isStart":true})});
            var Q34;
            Q34=makeQuery(id+"F8.boolean.opBoolean","COPY",EDGE,{"derivedFrom":makeQuery(id+"F8.opExtrude","CAP_EDGE",EDGE,{"disambiguationData":[OSD([sQuery(id+"F7.wireOp",EDGE,"E4.0.4.1")])],"isStart":true})});
            var Q35;
            Q35=makeQuery(id+"F8.boolean.opBoolean","COPY",EDGE,{"derivedFrom":makeQuery(id+"F8.opExtrude","CAP_EDGE",EDGE,{"disambiguationData":[OSD([sQuery(id+"F7.wireOp",EDGE,"E4.0.4.0")])],"isStart":true})});
            var Q36;
            Q36=makeQuery(id+"F8.boolean.opBoolean","COPY",EDGE,{"derivedFrom":makeQuery(id+"F8.opExtrude","CAP_EDGE",EDGE,{"disambiguationData":[OSD([sQuery(id+"F7.wireOp",EDGE,"E4.0.3.0")])],"isStart":true})});
            var Q37;
            Q37=makeQuery(id+"F8.boolean.opBoolean","COPY",EDGE,{"derivedFrom":makeQuery(id+"F8.opExtrude","CAP_EDGE",EDGE,{"disambiguationData":[OSD([sQuery(id+"F7.wireOp",EDGE,"E4.0.3.1")])],"isStart":true})});
            var Q38;
            Q38=makeQuery(id+"F8.boolean.opBoolean","COPY",EDGE,{"derivedFrom":makeQuery(id+"F8.opExtrude","CAP_EDGE",EDGE,{"disambiguationData":[OSD([sQuery(id+"F7.wireOp",EDGE,"E4.0.2.1")])],"isStart":true})});
            var Q39;
            Q39=makeQuery(id+"F8.boolean.opBoolean","COPY",EDGE,{"derivedFrom":makeQuery(id+"F8.opExtrude","CAP_EDGE",EDGE,{"disambiguationData":[OSD([sQuery(id+"F7.wireOp",EDGE,"E4.0.2.0")])],"isStart":true})});
            var Q40;
            Q40=makeQuery(id+"F8.boolean.opBoolean","COPY",EDGE,{"derivedFrom":makeQuery(id+"F8.opExtrude","CAP_EDGE",EDGE,{"disambiguationData":[OSD([sQuery(id+"F7.wireOp",EDGE,"E4.0.1.1")])],"isStart":true})});
            var Q41;
            Q41=makeQuery(id+"F8.boolean.opBoolean","COPY",EDGE,{"derivedFrom":makeQuery(id+"F8.opExtrude","CAP_EDGE",EDGE,{"disambiguationData":[OSD([sQuery(id+"F7.wireOp",EDGE,"E4.0.1.0")])],"isStart":true})});
            var Q42;
            Q42=makeQuery(id+"F8.boolean.opBoolean","COPY",EDGE,{"derivedFrom":makeQuery(id+"F8.opExtrude","CAP_EDGE",EDGE,{"disambiguationData":[OSD([sQuery(id+"F7.wireOp",EDGE,"E3.top")])],"isStart":true})});
            var Q43;
            Q43=makeQuery(id+"F8.boolean.opBoolean","COPY",EDGE,{"derivedFrom":makeQuery(id+"F8.opExtrude","CAP_EDGE",EDGE,{"disambiguationData":[OSD([sQuery(id+"F7.wireOp",EDGE,"E3.bottom")])],"isStart":false})});
            fillet(context, id + "F9", {"entities" : qUnion([Q0, Q1, Q2, Q3, Q4, Q5, Q6, Q7, Q8, Q9, Q10, Q11, Q12, Q13, Q14, Q15, Q16, Q17, Q18, Q19, Q20, Q21, Q22, Q23, Q24, Q25, Q26, Q27, Q28, Q29, Q30, Q31, Q32, Q33, Q34, Q35, Q36, Q37, Q38, Q39, Q40, Q41, Q42, Q43]), "tangentPropagation" : true, "radius" : 1.27 * mm, "defaultsChanged" : true, "vertexSettings" : [], "allowEdgeOverflow" : false});
        }
    });
